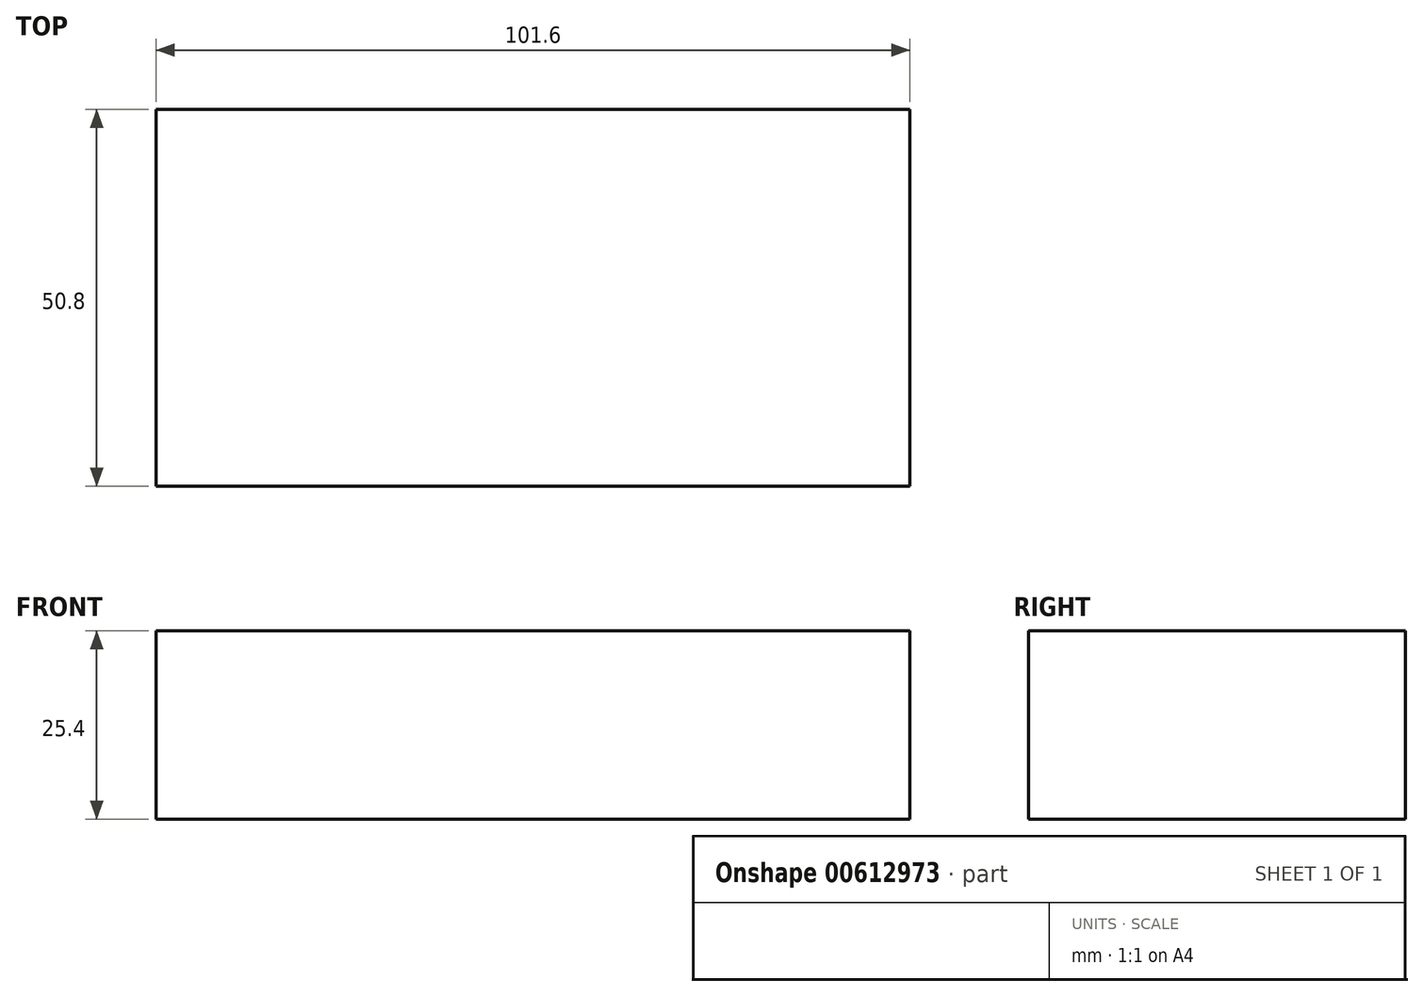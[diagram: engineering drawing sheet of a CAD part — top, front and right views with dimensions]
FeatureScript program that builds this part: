
annotation { "Feature Type Name" : "Feature", "Feature Type Description" : "" }
export const myFeature = defineFeature(function(context is Context, id is Id, definition is map)
    precondition{}
    {
        {
            var Q0;
            Q0=qCreatedBy(makeId("Top.planeOp"),FACE);
            var sketch = newSketch(context, id + "F0", { "sketchPlane" : qUnion([Q0])});
            skLineSegment(sketch, "E0.bottom", {"start": v(101.6, -60.66) * mm, "end": v(0, -60.66) * mm});
            skLineSegment(sketch, "E0.top", {"start": v(101.6, -9.86) * mm, "end": v(0, -9.86) * mm});
            skLineSegment(sketch, "E0.left", {"start": v(101.6, -60.66) * mm, "end": v(101.6, -9.86) * mm});
            skLineSegment(sketch, "E0.right", {"start": v(0, -60.66) * mm, "end": v(0, -9.86) * mm});
            skSolve(sketch);
        }
        {
            var Q0;
            Q0 = qSketchRegion(id + "F0", true);
            extrude(context, id + "F1", {"entities" : qUnion([Q0]), "depth" : 25.4 * mm, "offsetDistance" : 25.4 * mm});
        }
    });
